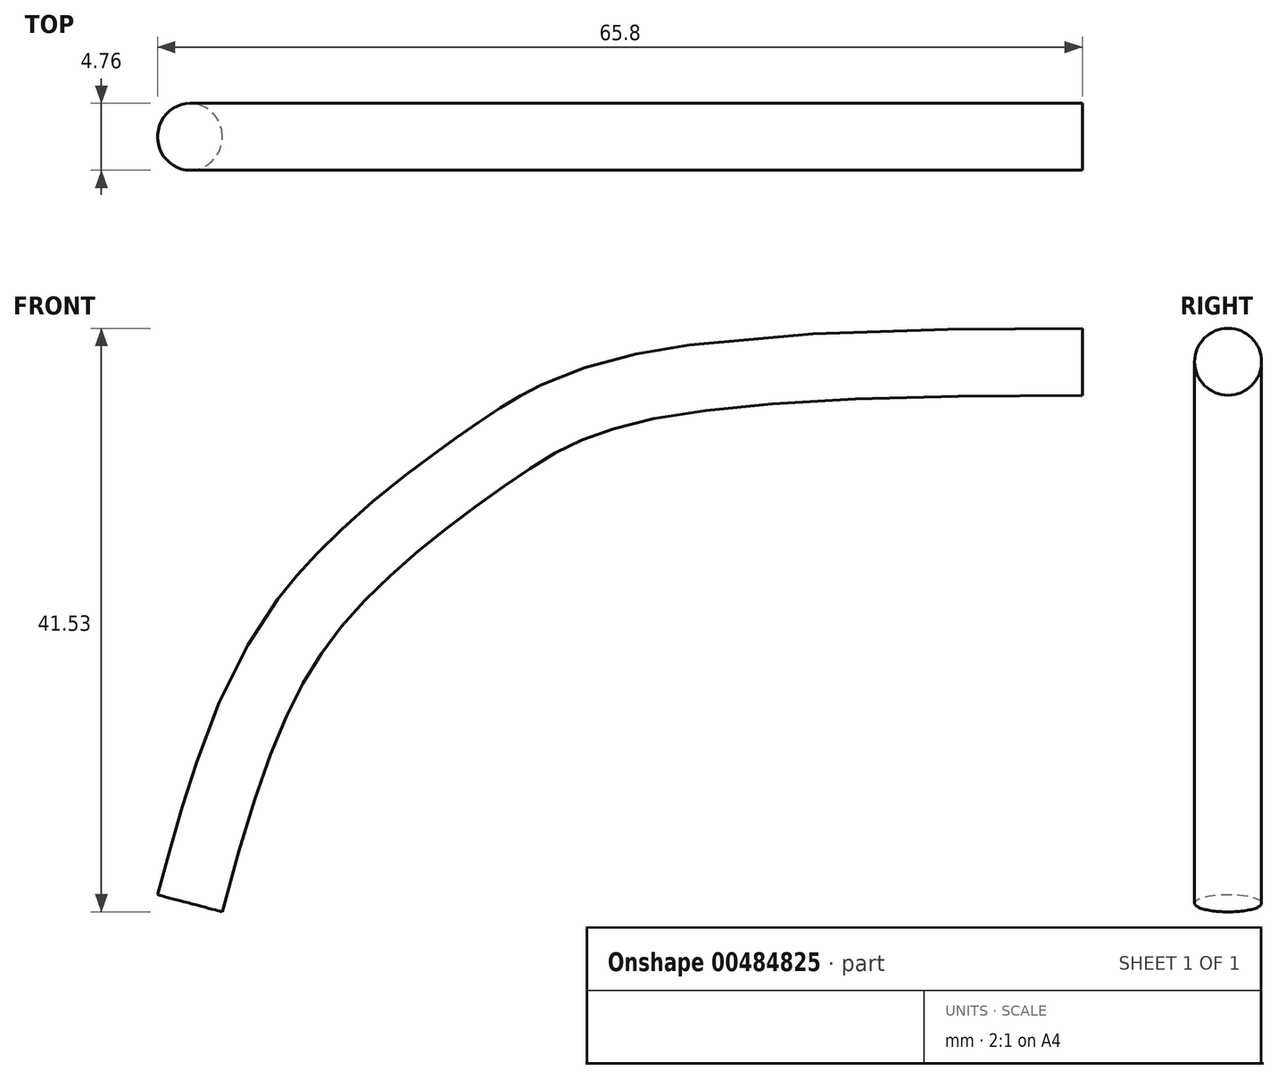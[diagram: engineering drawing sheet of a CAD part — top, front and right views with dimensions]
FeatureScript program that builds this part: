
annotation { "Feature Type Name" : "Feature", "Feature Type Description" : "" }
export const myFeature = defineFeature(function(context is Context, id is Id, definition is map)
    precondition{}
    {
        {
            var Q0;
            Q0=qCreatedBy(makeId("Front.planeOp"),FACE);
            var sketch = newSketch(context, id + "F0", { "sketchPlane" : qUnion([Q0])});
            skFitSpline(sketch, "E0", {"points": [v(0, 0) * mm, v(-42.08, -6.6) * mm, v(-54.06, -16.74) * mm, v(-63.5, -38.55) * mm], "startDerivative": vector(-223.91, 0) * mm, "endDerivative": vector(-28.3, -107.44) * mm});
            skSolve(sketch);
        }
        {
            var Q0;
            Q0=qCreatedBy(makeId("Right.planeOp"),FACE);
            var sketch = newSketch(context, id + "F1", { "sketchPlane" : qUnion([Q0])});
            skCircle(sketch, "E1", {"center": v(0, 0) * mm, "radius": 2.38 * mm});
            skSolve(sketch);
        }
        {
            var Q0;
            Q0=makeQuery(id+"F1.imprint","IMPRINT",FACE,{"disambiguationData":[TD([[makeQuery(id+"F1.imprint","IMPRINT",EDGE,{"derivedFrom":sQuery(id+"F1.wireOp",EDGE,"E1")}),1.0]])]});
            var Q1;
            Q1=sQuery(id+"F0.wireOp",EDGE,"E0");
            sweep(context, id + "F2", {"profiles" : qUnion([Q0]), "path" : qUnion([Q1])});
        }
    });
